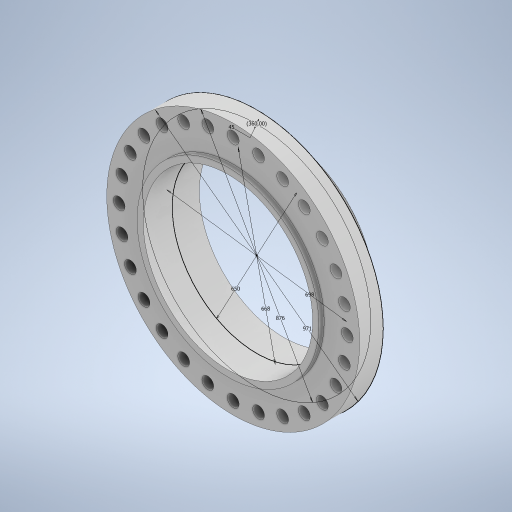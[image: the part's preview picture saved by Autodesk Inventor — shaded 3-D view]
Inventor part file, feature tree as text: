
AUTODESK INVENTOR PART (.ipt)
format: ipt  version: 2023 (Build 270158000, 158)  size: 348,672 bytes
history: native  units: mm
features: extrude x2, sketch x1, fillet x1
ambient origin geometry x8: Origin, YZ Plane, XZ Plane, XY Plane, X Axis, Y Axis, Z Axis, Center Point
bodies: Solido1 (feature_tree)
feature tree (4):
  sketch  "Schizzo1"
  extrude  "Estrusione1"  Depth=971.0mm
  extrude  "Estrusione2"  Depth=650.0mm
  fillet  "Raccordo1"  Radius=668.0mm
